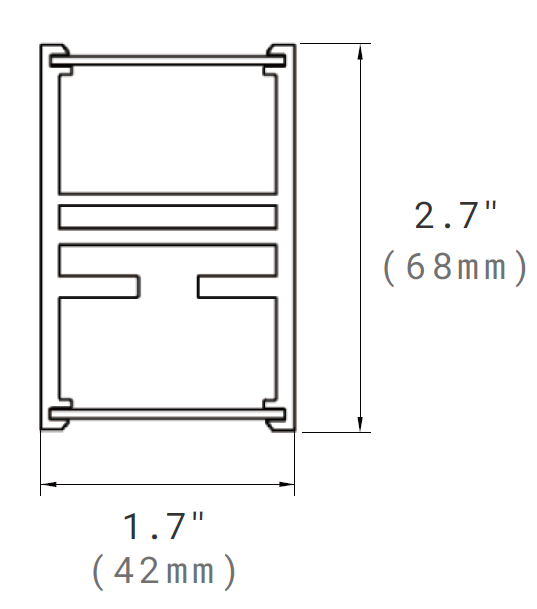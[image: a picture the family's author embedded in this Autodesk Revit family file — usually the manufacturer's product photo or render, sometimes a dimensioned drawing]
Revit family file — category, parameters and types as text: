
# Revit family: VRIO-ACPMK
name_source: partatom
category: Lighting Fixtures
units: mm (PartAtom-declared; Revit-internal decimal feet)

## family parameters
Cut with Voids When Loaded = Yes
Host = Face
Light Source = Yes
Maintain Annotation Orientation = No
Part Type = Normal
Room Calculation Point = No
Round Connector Dimension = Use Diameter
Shared = No

## types (9) — shared parameters
Beam Angle = 0.00°
CRI = 90
Color Filter = 16777215
Default Elevation = 0' - 0"
Dimming Lamp Color Temperature Shift = <None>
Input Voltage = 120-277V
Lamp = LED
Load Classification = Lighting
Manufacturer = Above All Lighting
Note = The actual cable count varies with the fixture size.
Power Factor = 0.9
Suspension = 3' - 0"
Tilt Angle = 90.00°

## per-type parameters (varying)
| type | D1 | Model | Photometric Web File | R | Wattage Comments | cable |
| VRIO-65W-3000K-ACPMK | 0' - 9 13/16" | VRIO-6524-30901-ACPMK-WH | VRIO_6524_30901.ies | 0' - 11 13/16" | 65W | 0' - 11 25/32" |
| VRIO-80W-3000K-ACPMK | 0' - 9 13/16" | VRIO-8035-30901-ACPMK-WH | VRIO_8035_30901.ies | 1' - 5 11/16" | 80W | 1' - 5 21/32" |
| VRIO-120W-3000K-ACPMK | 1' - 1 13/16" | VRIO-12047-30901-ACPMK-WH | VRIO_12047_30901.ies | 1' - 11 19/32" | 120W | 1' - 11 9/16" |
| VRIO-150W-3000K-ACPMK | 1' - 1 13/16" | VRIO-15079-30901-ACPMK-WH | generic | 3' - 3 13/32" | 150W | 3' - 3 3/8" |
| VRIO-200W-3000K-ACPMK | 1' - 5 11/16" | VRIO-20098-30901-ACPMK-WH | generic | 4' - 1 3/16" | 200W | 4' - 1 5/32" |
| VRIO-300W-3000K-ACPMK | 1' - 7 11/16" | VRIO-300118-30901-ACPMK-WH | generic | 4' - 11 1/16" | 300W | 4' - 11 1/32" |
| VRIO-400W-3000K-ACPMK | 1' - 11 19/32" | VRIO-400158-30901-ACPMK-WH | generic | 6' - 7" | 400W | 6' - 6 31/32" |
| VRIO-480W-3000K-ACPMK | 1' - 11 19/32" | VRIO-480197-30901-ACPMK-WH | generic | 8' - 2 7/16" | 480W | 8' - 2 13/32" |
| VRIO-135W-3000K-ACPMK | 1' - 1 13/16" | VRIO-13559-30901-ACPMK-WH | generic | 2' - 5 9/16" | 135W | 2' - 5 17/32" |

## geometry (parser evidence)
native form markers: Sweep x2
no freeform markers — native parametric forms only
